# Revit family: RUFO2 460xWSxH0350xx
name_source: partatom
category: Leuchten
units: mm (PartAtom-declared; Revit-internal decimal feet)

## family parameters
Basisbauteil = Fläche
Beim Laden mit Abzugskörper schneiden = Nein
Bemaßung runder Anschluss = Durchmesser verwenden
Gemeinsam genutzt = Nein
Lichtquelle = Ja
OmniClass-Nummer = 23.80.70.11
OmniClass-Titel = Luminaries for Internal Lighting
Raumberechnungspunkt = Nein
Teiletyp = Normal

## types (18) — shared parameters
Baugruppenkennzeichen = D5020200
Datei für fotometrisches Netz = RUFO2_460_H.IES
Emissionsform beim Rendern sichtbar = Nein
Farbfilter = 16777215
Farbtemperaturverschiebung bei Dämpfen der Lampe = <Keine Auswahl>
Hersteller = RIDI Leuchten GmbH
Lampe = LED
Neigungswinkel = 90.00°
URL = www.ridi.de
Von Kreisdurchmesser aussenden = 464 mm  [stored 1.52231 ft]
brand = RIDI
conformity mark = CE
electrical safety class = 1
height = 120 mm  [stored 0.393701 ft]
ingress protection (IP) code = IP40
length = 464 mm  [stored 1.52231 ft]
nominal frequency = 50-60Hz
nominal voltage = 230
voltage type (AC, DC, UC) = AC
width = 464 mm  [stored 1.52231 ft]
zero-valued in all types: Vorgabe-Ansicht

## per-type parameters (varying)
| type | Modell | Scheinlast | rated input power | weight |
| RUFO2 460NDWS840H0350 | 0420845 | 27 VA | 27 | 1,81 kg |
| RUFO2 460NDWS840H0350-RS | 0420845//396 | 27 VA | 27 | 1,85 kg |
| RUFO2 460NDWS830H0350 | 0420851 | 27 VA | 27 | 1,81 kg |
| RUFO2 460NDWS830H0350-RS | 0420851//396 | 27 VA | 27 | 1,85 kg |
| RUFO2 460NDWS840H0350-IK | 0420857 | 27 VA | 27 | 1,81 kg |
| RUFO2 460NDWS840H0350-IK-EDS3 | 0420857//377 | 27 VA | 27 | 2 kg |
| RUFO2 460NDWS840H0350-IK-RS | 0420857//377 | 27 VA | 27 | 1,85 kg |
| RUFO2 460NDWS830H0350-IK | 0420863 | 27 VA | 27 | 1,81 kg |
| RUFO2 460NDWS830H0350-IK-EDS3 | 0420863//377 | 27 VA | 27 | 2 kg |
| RUFO2 460NDWS830H0350-IK-RS | 0420863//396 | 27 VA | 27 | 1,85 kg |
| RUFO2 460DAWS840H0350 | 0430845 | 27 VA | 27 | 1,85 kg |
| RUFO2 460DAWS830H0350 | 0430851 | 27 VA | 27 | 1,85 kg |
| RUFO2 460DAWS840H0350-IK | 0430857 | 27 VA | 27 | 1,85 kg |
| RUFO2 460DAWS830H0350-IK | 0430863 | 27 VA | 27 | 1,85 kg |
| RUFO2 460NDWS840H0350-2K | 0420846 | 24 VA | 24 | 1,85 kg |
| RUFO2 460NDWS830H0350-2K | 0420852 | 24 VA | 24 | 1,85 kg |
| RUFO2 460NDWS840H0350-IK-2K | 0420858 | 24 VA | 24 | 1,82 kg |
| RUFO2 460NDWS830H0350-IK-2K | 0420864 | 24 VA | 24 | 1,85 kg |

note: column(s) folded — value = type name in every type: product name

note: [stored X ft] marks values corroborated as IEEE doubles in the binary element streams (Revit-internal decimal feet)
